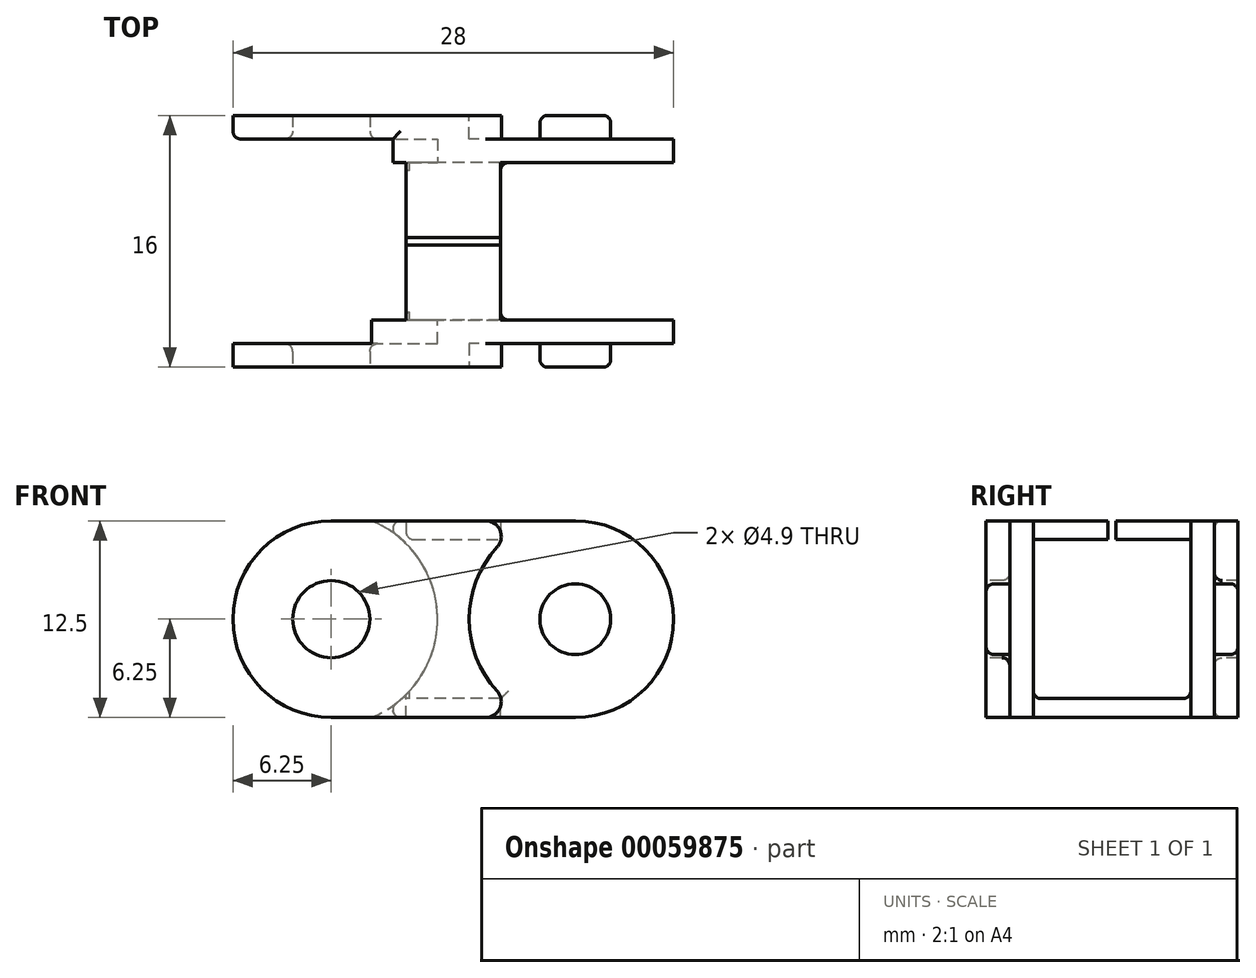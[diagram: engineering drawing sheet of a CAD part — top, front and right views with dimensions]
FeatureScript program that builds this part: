
annotation { "Feature Type Name" : "Feature", "Feature Type Description" : "" }
export const myFeature = defineFeature(function(context is Context, id is Id, definition is map)
    precondition{}
    {
        {
            var Q0;
            Q0=qCreatedBy(makeId("Top.planeOp"),FACE);
            var sketch = newSketch(context, id + "F0", { "sketchPlane" : qUnion([Q0])});
            skLineSegment(sketch, "E0.rect.bottom", {"start": v(14, -8) * mm, "end": v(-14, -8) * mm});
            skLineSegment(sketch, "E0.rect.top", {"start": v(14, 8) * mm, "end": v(-14, 8) * mm});
            skLineSegment(sketch, "E0.rect.left", {"start": v(14, -8) * mm, "end": v(14, 8) * mm});
            skLineSegment(sketch, "E0.rect.right", {"start": v(-14, -8) * mm, "end": v(-14, 8) * mm});
            skPoint(sketch, "E0.rect.middle", {"position": v(0, 0) * mm});
            skSolve(sketch);
        }
        {
            var Q0;
            Q0=qSketchRegion(id+"F0",true);
            extrude(context, id + "F1", {"entities" : qUnion([Q0]), "endBound" : BoundingType.SYMMETRIC, "depth" : 12.5 * mm});
        }
        {
            var Q0;
            Q0=makeQuery(id+"F1.opExtrude","CAP_EDGE",EDGE,{"disambiguationData":[OSD([sQuery(id+"F0.wireOp",EDGE,"E0.rect.right")])],"isStart":false});
            var Q1;
            Q1=makeQuery(id+"F1.opExtrude","CAP_EDGE",EDGE,{"disambiguationData":[OSD([sQuery(id+"F0.wireOp",EDGE,"E0.rect.right")])],"isStart":true});
            var Q2;
            Q2=makeQuery(id+"F1.opExtrude","CAP_EDGE",EDGE,{"disambiguationData":[OSD([sQuery(id+"F0.wireOp",EDGE,"E0.rect.left")])],"isStart":false});
            var Q3;
            Q3=makeQuery(id+"F1.opExtrude","CAP_EDGE",EDGE,{"disambiguationData":[OSD([sQuery(id+"F0.wireOp",EDGE,"E0.rect.left")])],"isStart":true});
            fillet(context, id + "F2", {"entities" : qUnion([Q0, Q1, Q2, Q3]), "radius" : 6.25 * mm, "tangentPropagation" : true, "allowEdgeOverflow" : false});
        }
        {
            var Q0;
            Q0=makeQuery(id+"F1.opExtrude","CAP_FACE",FACE,{"disambiguationData":[OSD([sQuery(id+"F0.wireOp",EDGE,"E0.rect.bottom"),sQuery(id+"F0.wireOp",EDGE,"E0.rect.top"),sQuery(id+"F0.wireOp",EDGE,"E0.rect.left"),sQuery(id+"F0.wireOp",EDGE,"E0.rect.right")])],"isStart":false});
            var Q1;
            {var subQ0=sQuery(id+"F0.wireOp",EDGE,"E0.rect.right");Q1=makeQuery(id+"F2.opFillet","BLEND_FACE",FACE,{"disambiguationData":[OSD([subQ0]),TDD([makeQuery(id+"F1.opExtrude","CAP_EDGE",EDGE,{"disambiguationData":[OSD([subQ0])],"isStart":false})])]});}
            var Q2;
            Q2=makeQuery(id+"F1.opExtrude","SWEPT_FACE",FACE,{"disambiguationData":[OSD([sQuery(id+"F0.wireOp",EDGE,"E0.rect.right")])]});
            var Q3;
            {var subQ0=sQuery(id+"F0.wireOp",EDGE,"E0.rect.right");Q3=makeQuery(id+"F2.opFillet","BLEND_FACE",FACE,{"disambiguationData":[OSD([subQ0]),TDD([makeQuery(id+"F1.opExtrude","CAP_EDGE",EDGE,{"disambiguationData":[OSD([subQ0])],"isStart":true})])]});}
            var Q4;
            {var subQ0=sQuery(id+"F0.wireOp",EDGE,"E0.rect.left");Q4=makeQuery(id+"F2.opFillet","BLEND_FACE",FACE,{"disambiguationData":[OSD([subQ0]),TDD([makeQuery(id+"F1.opExtrude","CAP_EDGE",EDGE,{"disambiguationData":[OSD([subQ0])],"isStart":false})])]});}
            var Q5;
            Q5=makeQuery(id+"F1.opExtrude","SWEPT_FACE",FACE,{"disambiguationData":[OSD([sQuery(id+"F0.wireOp",EDGE,"E0.rect.left")])]});
            var Q6;
            {var subQ0=sQuery(id+"F0.wireOp",EDGE,"E0.rect.left");Q6=makeQuery(id+"F2.opFillet","BLEND_FACE",FACE,{"disambiguationData":[OSD([subQ0]),TDD([makeQuery(id+"F1.opExtrude","CAP_EDGE",EDGE,{"disambiguationData":[OSD([subQ0])],"isStart":true})])]});}
            shell(context, id + "F3", {"entities" : qUnion([Q0, Q1, Q2, Q3, Q4, Q5, Q6]), "thickness" : 3 * mm});
        }
        {
            var Q0;
            {var subQ0=sQuery(id+"F0.wireOp",EDGE,"E0.rect.bottom");var subQ1=sQuery(id+"F0.wireOp",EDGE,"E0.rect.top");var subQ2=sQuery(id+"F0.wireOp",EDGE,"E0.rect.left");var subQ3=sQuery(id+"F0.wireOp",EDGE,"E0.rect.right");Q0=makeQuery(id+"F3.opShell","OFFSET_FACE",FACE,{"disambiguationData":[OSD([subQ0,subQ1,subQ2,subQ3]),TDD([makeQuery(id+"F1.opExtrude","CAP_FACE",FACE,{"disambiguationData":[OSD([subQ0,subQ1,subQ2,subQ3])],"isStart":true})])]});}
            var sketch = newSketch(context, id + "F4", { "sketchPlane" : qUnion([Q0])});
            skLineSegment(sketch, "E1.bottom", {"start": v(-7.75, -5) * mm, "end": v(-3, -5) * mm});
            skLineSegment(sketch, "E1.top", {"start": v(-7.75, 5) * mm, "end": v(-3, 5) * mm});
            skLineSegment(sketch, "E1.left", {"start": v(-7.75, -5) * mm, "end": v(-7.75, 5) * mm});
            skLineSegment(sketch, "E1.right", {"start": v(-3, -5) * mm, "end": v(-3, 5) * mm});
            skLineSegment(sketch, "E2.bottom", {"start": v(7.75, -5) * mm, "end": v(3, -5) * mm});
            skLineSegment(sketch, "E2.top", {"start": v(7.75, 5) * mm, "end": v(3, 5) * mm});
            skLineSegment(sketch, "E2.left", {"start": v(7.75, -5) * mm, "end": v(7.75, 5) * mm});
            skLineSegment(sketch, "E2.right", {"start": v(3, -5) * mm, "end": v(3, 5) * mm});
            skSolve(sketch);
        }
        {
            var Q0;
            Q0=qSketchRegion(id+"F4",true);
            extrude(context, id + "F5", {"entities" : qUnion([Q0]), "operationType" : NewBodyOperationType.REMOVE, "oppositeDirection" : true, "depth" : 25 * mm});
        }
        {
            var Q0;
            Q0=makeQuery(id+"F5.boolean.opBoolean","COPY",FACE,{"derivedFrom":makeQuery(id+"F5.opExtrude","SWEPT_FACE",FACE,{"disambiguationData":[OSD([sQuery(id+"F4.wireOp",EDGE,"E1.right")])]})});
            var sketch = newSketch(context, id + "F6", { "sketchPlane" : qUnion([Q0])});
            skLineSegment(sketch, "E3.bottom", {"start": v(-5, -3.25) * mm, "end": v(5, -3.25) * mm});
            skLineSegment(sketch, "E3.top", {"start": v(-5, -5.05) * mm, "end": v(5, -5.05) * mm});
            skLineSegment(sketch, "E3.left", {"start": v(-5, -3.25) * mm, "end": v(-5, -5.05) * mm});
            skLineSegment(sketch, "E3.right", {"start": v(5, -3.25) * mm, "end": v(5, -5.05) * mm});
            skSolve(sketch);
        }
        {
            var Q0;
            Q0=qSketchRegion(id+"F6",true);
            extrude(context, id + "F7", {"entities" : qUnion([Q0]), "operationType" : NewBodyOperationType.REMOVE, "oppositeDirection" : true, "depth" : 25 * mm});
        }
        {
            var Q0;
            Q0=makeQuery(id+"F1.opExtrude","CAP_FACE",FACE,{"disambiguationData":[OSD([sQuery(id+"F0.wireOp",EDGE,"E0.rect.bottom"),sQuery(id+"F0.wireOp",EDGE,"E0.rect.top"),sQuery(id+"F0.wireOp",EDGE,"E0.rect.left"),sQuery(id+"F0.wireOp",EDGE,"E0.rect.right")])],"isStart":false});
            var sketch = newSketch(context, id + "F8", { "sketchPlane" : qUnion([Q0])});
            skLineSegment(sketch, "E4.bottom", {"start": v(-3, 5) * mm, "end": v(3, 5) * mm});
            skLineSegment(sketch, "E4.top", {"start": v(-3, -5) * mm, "end": v(3, -5) * mm});
            skLineSegment(sketch, "E4.left", {"start": v(-3, 5) * mm, "end": v(-3, -5) * mm});
            skLineSegment(sketch, "E4.right", {"start": v(3, 5) * mm, "end": v(3, -5) * mm});
            skSolve(sketch);
        }
        {
            var Q0;
            Q0=qSketchRegion(id+"F8",true);
            extrude(context, id + "F9", {"entities" : qUnion([Q0]), "operationType" : NewBodyOperationType.ADD, "oppositeDirection" : true, "depth" : 1.2 * mm});
        }
        {
            var Q0;
            Q0=makeQuery(id+"F1.opExtrude","SWEPT_FACE",FACE,{"disambiguationData":[OSD([sQuery(id+"F0.wireOp",EDGE,"E0.rect.bottom")])]});
            var sketch = newSketch(context, id + "F10", { "sketchPlane" : qUnion([Q0])});
            skCircle(sketch, "E5", {"center": v(7.75, 0) * mm, "radius": 6.75 * mm});
            skSolve(sketch);
        }
        {
            var Q0;
            Q0=qSketchRegion(id+"F10",true);
            extrude(context, id + "F11", {"entities" : qUnion([Q0]), "operationType" : NewBodyOperationType.REMOVE, "oppositeDirection" : true, "depth" : 1.5 * mm});
        }
        {
            var Q0;
            Q0=makeQuery(id+"F1.opExtrude","SWEPT_FACE",FACE,{"disambiguationData":[OSD([sQuery(id+"F0.wireOp",EDGE,"E0.rect.top")])]});
            var sketch = newSketch(context, id + "F12", { "sketchPlane" : qUnion([Q0])});
            skCircle(sketch, "E6", {"center": v(-7.75, 0) * mm, "radius": 6.75 * mm});
            skSolve(sketch);
        }
        {
            var Q0;
            Q0=qSketchRegion(id+"F12",true);
            extrude(context, id + "F13", {"entities" : qUnion([Q0]), "operationType" : NewBodyOperationType.REMOVE, "oppositeDirection" : true, "depth" : 1.5 * mm});
        }
        {
            var Q0;
            {var subQ0=sQuery(id+"F0.wireOp",EDGE,"E0.rect.bottom");var subQ1=sQuery(id+"F0.wireOp",EDGE,"E0.rect.top");var subQ2=sQuery(id+"F0.wireOp",EDGE,"E0.rect.left");var subQ3=sQuery(id+"F0.wireOp",EDGE,"E0.rect.right");var subQ4=makeQuery(id+"F1.opExtrude","CAP_FACE",FACE,{"disambiguationData":[OSD([subQ0,subQ1,subQ2,subQ3])],"isStart":false});Q0=makeQuery(id+"F11.boolean.opBoolean","INTERSECT",EDGE,{"derivedFrom":[makeQuery(id+"FRDs2wFj56Co6Q4_1.boolean.opBoolean","MERGE",FACE,{"derivedFrom":[makeQuery(id+"F3.opShell","OFFSET_FACE",FACE,{"disambiguationData":[OSD([subQ0,subQ1,subQ2,subQ3]),TDD([subQ4])]}),subQ4,makeQuery(id+"FRDs2wFj56Co6Q4_1.opExtrude","CAP_FACE",FACE,{"disambiguationData":[OSD([sQuery(id+"F8wkNr267Ss34zO_1.wireOp",EDGE,"6609082b-c965-4ff1-a180-b40e3fbcedff.bottom"),sQuery(id+"F8wkNr267Ss34zO_1.wireOp",EDGE,"6609082b-c965-4ff1-a180-b40e3fbcedff.top"),sQuery(id+"F8wkNr267Ss34zO_1.wireOp",EDGE,"6609082b-c965-4ff1-a180-b40e3fbcedff.left"),sQuery(id+"F8wkNr267Ss34zO_1.wireOp",EDGE,"6609082b-c965-4ff1-a180-b40e3fbcedff.right")])],"isStart":true})]}),makeQuery(id+"F11.opExtrude","SWEPT_FACE",FACE,{"disambiguationData":[OSD([sQuery(id+"F10.wireOp",EDGE,"E5")])]})]});}
            var Q1;
            Q1=makeQuery(id+"F11.boolean.opBoolean","INTERSECT",EDGE,{"derivedFrom":[makeQuery(id+"F1.opExtrude","CAP_FACE",FACE,{"disambiguationData":[OSD([sQuery(id+"F0.wireOp",EDGE,"E0.rect.bottom"),sQuery(id+"F0.wireOp",EDGE,"E0.rect.top"),sQuery(id+"F0.wireOp",EDGE,"E0.rect.left"),sQuery(id+"F0.wireOp",EDGE,"E0.rect.right")])],"isStart":true}),makeQuery(id+"F11.opExtrude","SWEPT_FACE",FACE,{"disambiguationData":[OSD([sQuery(id+"F10.wireOp",EDGE,"E5")])]})]});
            var Q2;
            {var subQ0=sQuery(id+"F0.wireOp",EDGE,"E0.rect.bottom");var subQ1=sQuery(id+"F0.wireOp",EDGE,"E0.rect.top");var subQ2=sQuery(id+"F0.wireOp",EDGE,"E0.rect.left");var subQ3=sQuery(id+"F0.wireOp",EDGE,"E0.rect.right");var subQ4=makeQuery(id+"F1.opExtrude","CAP_FACE",FACE,{"disambiguationData":[OSD([subQ0,subQ1,subQ2,subQ3])],"isStart":false});Q2=makeQuery(id+"F13.boolean.opBoolean","INTERSECT",EDGE,{"derivedFrom":[makeQuery(id+"FRDs2wFj56Co6Q4_1.boolean.opBoolean","MERGE",FACE,{"derivedFrom":[makeQuery(id+"F3.opShell","OFFSET_FACE",FACE,{"disambiguationData":[OSD([subQ0,subQ1,subQ2,subQ3]),TDD([subQ4])]}),subQ4,makeQuery(id+"FRDs2wFj56Co6Q4_1.opExtrude","CAP_FACE",FACE,{"disambiguationData":[OSD([sQuery(id+"F8wkNr267Ss34zO_1.wireOp",EDGE,"6609082b-c965-4ff1-a180-b40e3fbcedff.bottom"),sQuery(id+"F8wkNr267Ss34zO_1.wireOp",EDGE,"6609082b-c965-4ff1-a180-b40e3fbcedff.top"),sQuery(id+"F8wkNr267Ss34zO_1.wireOp",EDGE,"6609082b-c965-4ff1-a180-b40e3fbcedff.left"),sQuery(id+"F8wkNr267Ss34zO_1.wireOp",EDGE,"6609082b-c965-4ff1-a180-b40e3fbcedff.right")])],"isStart":true})]}),makeQuery(id+"F13.opExtrude","SWEPT_FACE",FACE,{"disambiguationData":[OSD([sQuery(id+"F12.wireOp",EDGE,"E6")])]})]});}
            var Q3;
            Q3=makeQuery(id+"F13.boolean.opBoolean","INTERSECT",EDGE,{"derivedFrom":[makeQuery(id+"F1.opExtrude","CAP_FACE",FACE,{"disambiguationData":[OSD([sQuery(id+"F0.wireOp",EDGE,"E0.rect.bottom"),sQuery(id+"F0.wireOp",EDGE,"E0.rect.top"),sQuery(id+"F0.wireOp",EDGE,"E0.rect.left"),sQuery(id+"F0.wireOp",EDGE,"E0.rect.right")])],"isStart":true}),makeQuery(id+"F13.opExtrude","SWEPT_FACE",FACE,{"disambiguationData":[OSD([sQuery(id+"F12.wireOp",EDGE,"E6")])]})]});
            var Q4;
            {var subQ0=sQuery(id+"F0.wireOp",EDGE,"E0.rect.left");var subQ1=sQuery(id+"F0.wireOp",EDGE,"E0.rect.bottom");var subQ2=sQuery(id+"F0.wireOp",EDGE,"E0.rect.top");var subQ3=sQuery(id+"F0.wireOp",EDGE,"E0.rect.right");var subQ4=makeQuery(id+"F1.opExtrude","CAP_FACE",FACE,{"disambiguationData":[OSD([subQ1,subQ2,subQ0,subQ3])],"isStart":false});Q4=makeQuery(id+"F11.boolean.opBoolean","SPLIT",EDGE,{"disambiguationData":[TD([makeQuery(id+"F1.opExtrude","SWEPT_FACE",FACE,{"disambiguationData":[OSD([subQ1])]})])],"derivedFrom":makeQuery(id+"F2.opFillet","BLEND_EDGE",EDGE,{"blendedFrom":[makeQuery(id+"F1.opExtrude","CAP_EDGE",EDGE,{"disambiguationData":[OSD([subQ0])],"isStart":false}),subQ4],"blendedInto":[subQ4]})});}
            var Q5;
            {var subQ0=sQuery(id+"F0.wireOp",EDGE,"E0.rect.bottom");var subQ1=sQuery(id+"F0.wireOp",EDGE,"E0.rect.top");var subQ2=sQuery(id+"F0.wireOp",EDGE,"E0.rect.left");var subQ3=sQuery(id+"F0.wireOp",EDGE,"E0.rect.right");var subQ4=makeQuery(id+"F1.opExtrude","CAP_FACE",FACE,{"disambiguationData":[OSD([subQ0,subQ1,subQ2,subQ3])],"isStart":true});Q5=makeQuery(id+"F11.boolean.opBoolean","SPLIT",EDGE,{"disambiguationData":[TD([makeQuery(id+"F1.opExtrude","SWEPT_FACE",FACE,{"disambiguationData":[OSD([subQ0])]})])],"derivedFrom":makeQuery(id+"F3.opShell","OFFSET_EDGE",EDGE,{"disambiguationData":[OSD([subQ0,subQ1,subQ2,subQ3]),TDD([makeQuery(id+"F2.opFillet","BLEND_EDGE",EDGE,{"blendedFrom":[makeQuery(id+"F1.opExtrude","CAP_EDGE",EDGE,{"disambiguationData":[OSD([subQ2])],"isStart":true}),subQ4],"blendedInto":[subQ4]})]),OD(0.0)]})});}
            var Q6;
            {var subQ0=sQuery(id+"F0.wireOp",EDGE,"E0.rect.bottom");var subQ1=sQuery(id+"F0.wireOp",EDGE,"E0.rect.top");var subQ2=sQuery(id+"F0.wireOp",EDGE,"E0.rect.left");var subQ3=sQuery(id+"F0.wireOp",EDGE,"E0.rect.right");var subQ4=makeQuery(id+"F1.opExtrude","CAP_FACE",FACE,{"disambiguationData":[OSD([subQ0,subQ1,subQ2,subQ3])],"isStart":false});Q6=makeQuery(id+"F13.boolean.opBoolean","SPLIT",EDGE,{"disambiguationData":[TD([makeQuery(id+"F1.opExtrude","SWEPT_FACE",FACE,{"disambiguationData":[OSD([subQ1])]})])],"derivedFrom":makeQuery(id+"F3.opShell","OFFSET_EDGE",EDGE,{"disambiguationData":[OSD([subQ0,subQ1,subQ2,subQ3]),TDD([makeQuery(id+"F2.opFillet","BLEND_EDGE",EDGE,{"blendedFrom":[makeQuery(id+"F1.opExtrude","CAP_EDGE",EDGE,{"disambiguationData":[OSD([subQ2])],"isStart":false}),subQ4],"blendedInto":[subQ4]})])]})});}
            var Q7;
            {var subQ0=sQuery(id+"F0.wireOp",EDGE,"E0.rect.left");var subQ1=sQuery(id+"F0.wireOp",EDGE,"E0.rect.top");var subQ2=makeQuery(id+"F1.opExtrude","CAP_FACE",FACE,{"disambiguationData":[OSD([sQuery(id+"F0.wireOp",EDGE,"E0.rect.bottom"),subQ1,subQ0,sQuery(id+"F0.wireOp",EDGE,"E0.rect.right")])],"isStart":true});Q7=makeQuery(id+"F13.boolean.opBoolean","SPLIT",EDGE,{"disambiguationData":[TD([makeQuery(id+"F1.opExtrude","SWEPT_FACE",FACE,{"disambiguationData":[OSD([subQ1])]})])],"derivedFrom":makeQuery(id+"F2.opFillet","BLEND_EDGE",EDGE,{"blendedFrom":[makeQuery(id+"F1.opExtrude","CAP_EDGE",EDGE,{"disambiguationData":[OSD([subQ0])],"isStart":true}),subQ2],"blendedInto":[subQ2]})});}
            fillet(context, id + "F14", {"entities" : qUnion([Q0, Q1, Q2, Q3, Q4, Q5, Q6, Q7]), "radius" : 1 * mm, "tangentPropagation" : true, "allowEdgeOverflow" : false});
        }
        {
            var Q0;
            Q0=makeQuery(id+"F11.boolean.opBoolean","COPY",FACE,{"derivedFrom":makeQuery(id+"F11.opExtrude","CAP_FACE",FACE,{"disambiguationData":[OSD([sQuery(id+"F10.wireOp",EDGE,"E5")])],"isStart":false})});
            var sketch = newSketch(context, id + "F15", { "sketchPlane" : qUnion([Q0])});
            skCircle(sketch, "E7", {"center": v(7.75, 0) * mm, "radius": 2.25 * mm});
            skSolve(sketch);
        }
        {
            var Q0;
            Q0=qSketchRegion(id+"F15",true);
            extrude(context, id + "F16", {"entities" : qUnion([Q0]), "operationType" : NewBodyOperationType.ADD, "depth" : 1.5 * mm});
        }
        {
            var Q0;
            Q0=makeQuery(id+"F13.boolean.opBoolean","COPY",FACE,{"derivedFrom":makeQuery(id+"F13.opExtrude","CAP_FACE",FACE,{"disambiguationData":[OSD([sQuery(id+"F12.wireOp",EDGE,"E6")])],"isStart":false})});
            var sketch = newSketch(context, id + "F17", { "sketchPlane" : qUnion([Q0])});
            skCircle(sketch, "E8", {"center": v(-7.75, 0) * mm, "radius": 2.25 * mm});
            skSolve(sketch);
        }
        {
            var Q0;
            Q0=qSketchRegion(id+"F17",true);
            extrude(context, id + "F18", {"entities" : qUnion([Q0]), "operationType" : NewBodyOperationType.ADD, "depth" : 1.5 * mm});
        }
        {
            var Q0;
            Q0=makeQuery(id+"F1.opExtrude","SWEPT_FACE",FACE,{"disambiguationData":[OSD([sQuery(id+"F0.wireOp",EDGE,"E0.rect.bottom")])]});
            var sketch = newSketch(context, id + "F19", { "sketchPlane" : qUnion([Q0])});
            skCircle(sketch, "E9", {"center": v(-7.75, 0) * mm, "radius": 2.45 * mm});
            skSolve(sketch);
        }
        {
            var Q0;
            Q0=qSketchRegion(id+"F19",true);
            extrude(context, id + "F20", {"entities" : qUnion([Q0]), "operationType" : NewBodyOperationType.REMOVE, "endBound" : BoundingType.THROUGH_ALL, "oppositeDirection" : true, "depth" : 25 * mm});
        }
        {
            var Q0;
            Q0=makeQuery(id+"FHNYXm6BuEGCrrz_1.boolean.opBoolean","MERGE",FACE,{"derivedFrom":[makeQuery(id+"F3.opShell","OFFSET_FACE",FACE,{"disambiguationData":[OSD([sQuery(id+"F0.wireOp",EDGE,"E0.rect.top")])]}),makeQuery(id+"FHNYXm6BuEGCrrz_1.opExtrude","SWEPT_FACE",FACE,{"disambiguationData":[OSD([sQuery(id+"FrscQX9RS2ccQFD_1.wireOp",EDGE,"376541ee-2e4d-4804-9836-3ca692176c24.right")])]})]});
            var sketch = newSketch(context, id + "F21", { "sketchPlane" : qUnion([Q0])});
            skCircle(sketch, "E10", {"center": v(-7.75, 0) * mm, "radius": 6.75 * mm});
            skSolve(sketch);
        }
        {
            var Q0;
            Q0=qSketchRegion(id+"F21",true);
            extrude(context, id + "F22", {"entities" : qUnion([Q0]), "operationType" : NewBodyOperationType.REMOVE, "oppositeDirection" : true, "depth" : 1.5 * mm});
        }
        {
            var Q0;
            Q0=makeQuery(id+"FHNYXm6BuEGCrrz_1.boolean.opBoolean","MERGE",FACE,{"derivedFrom":[makeQuery(id+"F3.opShell","OFFSET_FACE",FACE,{"disambiguationData":[OSD([sQuery(id+"F0.wireOp",EDGE,"E0.rect.bottom")])]}),makeQuery(id+"FHNYXm6BuEGCrrz_1.opExtrude","SWEPT_FACE",FACE,{"disambiguationData":[OSD([sQuery(id+"FrscQX9RS2ccQFD_1.wireOp",EDGE,"376541ee-2e4d-4804-9836-3ca692176c24.left")])]})]});
            var sketch = newSketch(context, id + "F23", { "sketchPlane" : qUnion([Q0])});
            skCircle(sketch, "E11", {"center": v(7.75, 0) * mm, "radius": 6.75 * mm});
            skSolve(sketch);
        }
        {
            var Q0;
            Q0=qSketchRegion(id+"F23",true);
            extrude(context, id + "F24", {"entities" : qUnion([Q0]), "operationType" : NewBodyOperationType.REMOVE, "oppositeDirection" : true, "depth" : 1.5 * mm});
        }
        {
            var Q0;
            {var subQ0=sQuery(id+"F0.wireOp",EDGE,"E0.rect.bottom");var subQ1=sQuery(id+"F0.wireOp",EDGE,"E0.rect.top");var subQ2=sQuery(id+"F0.wireOp",EDGE,"E0.rect.left");var subQ3=sQuery(id+"F0.wireOp",EDGE,"E0.rect.right");var subQ4=makeQuery(id+"F1.opExtrude","CAP_FACE",FACE,{"disambiguationData":[OSD([subQ0,subQ1,subQ2,subQ3])],"isStart":false});Q0=makeQuery(id+"F22.boolean.opBoolean","INTERSECT",EDGE,{"derivedFrom":[makeQuery(id+"FRDs2wFj56Co6Q4_1.boolean.opBoolean","MERGE",FACE,{"derivedFrom":[makeQuery(id+"F3.opShell","OFFSET_FACE",FACE,{"disambiguationData":[OSD([subQ0,subQ1,subQ2,subQ3]),TDD([subQ4])]}),subQ4,makeQuery(id+"FRDs2wFj56Co6Q4_1.opExtrude","CAP_FACE",FACE,{"disambiguationData":[OSD([sQuery(id+"F8wkNr267Ss34zO_1.wireOp",EDGE,"6609082b-c965-4ff1-a180-b40e3fbcedff.bottom"),sQuery(id+"F8wkNr267Ss34zO_1.wireOp",EDGE,"6609082b-c965-4ff1-a180-b40e3fbcedff.top"),sQuery(id+"F8wkNr267Ss34zO_1.wireOp",EDGE,"6609082b-c965-4ff1-a180-b40e3fbcedff.left"),sQuery(id+"F8wkNr267Ss34zO_1.wireOp",EDGE,"6609082b-c965-4ff1-a180-b40e3fbcedff.right")])],"isStart":true})]}),makeQuery(id+"F22.opExtrude","SWEPT_FACE",FACE,{"disambiguationData":[OSD([sQuery(id+"F21.wireOp",EDGE,"E10")])]})]});}
            var Q1;
            Q1=makeQuery(id+"F22.boolean.opBoolean","INTERSECT",EDGE,{"derivedFrom":[makeQuery(id+"F1.opExtrude","CAP_FACE",FACE,{"disambiguationData":[OSD([sQuery(id+"F0.wireOp",EDGE,"E0.rect.bottom"),sQuery(id+"F0.wireOp",EDGE,"E0.rect.top"),sQuery(id+"F0.wireOp",EDGE,"E0.rect.left"),sQuery(id+"F0.wireOp",EDGE,"E0.rect.right")])],"isStart":true}),makeQuery(id+"F22.opExtrude","SWEPT_FACE",FACE,{"disambiguationData":[OSD([sQuery(id+"F21.wireOp",EDGE,"E10")])]})]});
            var Q2;
            {var subQ0=sQuery(id+"F0.wireOp",EDGE,"E0.rect.bottom");var subQ1=sQuery(id+"F0.wireOp",EDGE,"E0.rect.top");var subQ2=sQuery(id+"F0.wireOp",EDGE,"E0.rect.left");var subQ3=sQuery(id+"F0.wireOp",EDGE,"E0.rect.right");var subQ4=makeQuery(id+"F1.opExtrude","CAP_FACE",FACE,{"disambiguationData":[OSD([subQ0,subQ1,subQ2,subQ3])],"isStart":false});Q2=makeQuery(id+"F22.boolean.opBoolean","INTERSECT",EDGE,{"derivedFrom":[makeQuery(id+"FRDs2wFj56Co6Q4_1.boolean.opBoolean","MERGE",FACE,{"derivedFrom":[makeQuery(id+"F3.opShell","OFFSET_FACE",FACE,{"disambiguationData":[OSD([subQ0,subQ1,subQ2,subQ3]),TDD([subQ4])]}),subQ4,makeQuery(id+"FRDs2wFj56Co6Q4_1.opExtrude","CAP_FACE",FACE,{"disambiguationData":[OSD([sQuery(id+"F8wkNr267Ss34zO_1.wireOp",EDGE,"6609082b-c965-4ff1-a180-b40e3fbcedff.bottom"),sQuery(id+"F8wkNr267Ss34zO_1.wireOp",EDGE,"6609082b-c965-4ff1-a180-b40e3fbcedff.top"),sQuery(id+"F8wkNr267Ss34zO_1.wireOp",EDGE,"6609082b-c965-4ff1-a180-b40e3fbcedff.left"),sQuery(id+"F8wkNr267Ss34zO_1.wireOp",EDGE,"6609082b-c965-4ff1-a180-b40e3fbcedff.right")])],"isStart":true})]}),makeQuery(id+"F22.opExtrude","CAP_FACE",FACE,{"disambiguationData":[OSD([sQuery(id+"F21.wireOp",EDGE,"E10")])],"isStart":false})]});}
            var Q3;
            Q3=makeQuery(id+"F22.boolean.opBoolean","INTERSECT",EDGE,{"derivedFrom":[makeQuery(id+"F3.opShell","OFFSET_FACE",FACE,{"disambiguationData":[OSD([sQuery(id+"F0.wireOp",EDGE,"E0.rect.right")])]}),makeQuery(id+"F22.opExtrude","CAP_FACE",FACE,{"disambiguationData":[OSD([sQuery(id+"F21.wireOp",EDGE,"E10")])],"isStart":false})]});
            fillet(context, id + "F25", {"entities" : qUnion([Q0, Q1, Q2, Q3]), "radius" : 0.5 * mm, "tangentPropagation" : true, "allowEdgeOverflow" : false});
        }
        {
            var Q0;
            Q0=makeQuery(id+"F7.boolean.opBoolean","COPY",EDGE,{"derivedFrom":makeQuery(id+"F7.opExtrude","CAP_EDGE",EDGE,{"disambiguationData":[OSD([sQuery(id+"F6.wireOp",EDGE,"E3.top")])],"isStart":true})});
            var Q1;
            Q1=makeQuery(id+"F9.opExtrude","CAP_EDGE",EDGE,{"disambiguationData":[OSD([sQuery(id+"F8.wireOp",EDGE,"E4.left")])],"isStart":false});
            fillet(context, id + "F26", {"entities" : qUnion([Q0, Q1]), "radius" : 0.5 * mm, "allowEdgeOverflow" : false});
        }
        {
            var Q0;
            {var subQ0=sQuery(id+"F0.wireOp",EDGE,"E0.rect.bottom");var subQ1=sQuery(id+"F4.wireOp",EDGE,"E1.bottom");var subQ2=sQuery(id+"F6.wireOp",EDGE,"E3.top");var subQ3=sQuery(id+"F6.wireOp",EDGE,"E3.right");Q0=makeQuery(id+"F24.boolean.opBoolean","SPLIT",EDGE,{"disambiguationData":[TD([makeQuery(id+"F5.boolean.opBoolean","COPY",FACE,{"derivedFrom":makeQuery(id+"F5.opExtrude","SWEPT_FACE",FACE,{"disambiguationData":[OSD([sQuery(id+"F4.wireOp",EDGE,"E2.right")])]})})])],"derivedFrom":makeQuery(id+"F7.boolean.opBoolean","COPY",EDGE,{"derivedFrom":makeQuery(id+"F7.opExtrude","SWEPT_EDGE",EDGE,{"disambiguationData":[OSD([subQ0,subQ1,sQuery(id+"F4.wireOp",EDGE,"E1.right"),subQ2,subQ3])]})})});}
            var Q1;
            {var subQ0=sQuery(id+"F8.wireOp",EDGE,"E4.top");var subQ2=sQuery(id+"F8.wireOp",EDGE,"E4.right");Q1=makeQuery(id+"F24.boolean.opBoolean","SPLIT",EDGE,{"disambiguationData":[TD([makeQuery(id+"F9.opExtrude","SWEPT_FACE",FACE,{"disambiguationData":[OSD([subQ2])]})])],"derivedFrom":makeQuery(id+"F9.opExtrude","CAP_EDGE",EDGE,{"disambiguationData":[OSD([subQ0])],"isStart":false})});}
            var Q2;
            {var subQ0=sQuery(id+"F0.wireOp",EDGE,"E0.rect.top");var subQ1=sQuery(id+"F4.wireOp",EDGE,"E1.top");var subQ2=sQuery(id+"F6.wireOp",EDGE,"E3.top");var subQ3=sQuery(id+"F6.wireOp",EDGE,"E3.left");Q2=makeQuery(id+"F22.boolean.opBoolean","SPLIT",EDGE,{"disambiguationData":[TD([makeQuery(id+"F5.boolean.opBoolean","COPY",FACE,{"derivedFrom":makeQuery(id+"F5.opExtrude","SWEPT_FACE",FACE,{"disambiguationData":[OSD([sQuery(id+"F4.wireOp",EDGE,"E2.right")])]})})])],"derivedFrom":makeQuery(id+"F7.boolean.opBoolean","COPY",EDGE,{"derivedFrom":makeQuery(id+"F7.opExtrude","SWEPT_EDGE",EDGE,{"disambiguationData":[OSD([subQ0,subQ1,sQuery(id+"F4.wireOp",EDGE,"E1.right"),subQ2,subQ3])]})})});}
            var Q3;
            {var subQ0=sQuery(id+"F8.wireOp",EDGE,"E4.bottom");var subQ2=sQuery(id+"F8.wireOp",EDGE,"E4.right");Q3=makeQuery(id+"F22.boolean.opBoolean","SPLIT",EDGE,{"disambiguationData":[TD([makeQuery(id+"F9.opExtrude","SWEPT_FACE",FACE,{"disambiguationData":[OSD([subQ2])]})])],"derivedFrom":makeQuery(id+"F9.opExtrude","CAP_EDGE",EDGE,{"disambiguationData":[OSD([subQ0])],"isStart":false})});}
            var Q4;
            Q4=makeQuery(id+"F9.opExtrude","SWEPT_EDGE",EDGE,{"disambiguationData":[OSD([sQuery(id+"F0.wireOp",EDGE,"E0.rect.top"),sQuery(id+"F8.wireOp",EDGE,"E4.bottom"),sQuery(id+"F8.wireOp",EDGE,"E4.right")])]});
            var Q5;
            Q5=makeQuery(id+"F9.opExtrude","SWEPT_EDGE",EDGE,{"disambiguationData":[OSD([sQuery(id+"F8.wireOp",EDGE,"E4.top"),sQuery(id+"F8.wireOp",EDGE,"E4.right")])]});
            var Q6;
            Q6=makeQuery(id+"F5.boolean.opBoolean","COPY",EDGE,{"derivedFrom":makeQuery(id+"F5.opExtrude","SWEPT_EDGE",EDGE,{"disambiguationData":[OSD([sQuery(id+"F0.wireOp",EDGE,"E0.rect.bottom"),sQuery(id+"F4.wireOp",EDGE,"E2.bottom"),sQuery(id+"F4.wireOp",EDGE,"E2.right")])]})});
            var Q7;
            Q7=makeQuery(id+"F5.boolean.opBoolean","COPY",EDGE,{"derivedFrom":makeQuery(id+"F5.opExtrude","SWEPT_EDGE",EDGE,{"disambiguationData":[OSD([sQuery(id+"F0.wireOp",EDGE,"E0.rect.top"),sQuery(id+"F4.wireOp",EDGE,"E2.top"),sQuery(id+"F4.wireOp",EDGE,"E2.right")])]})});
            fillet(context, id + "F27", {"entities" : qUnion([Q0, Q1, Q2, Q3, Q4, Q5, Q6, Q7]), "radius" : 0.5 * mm, "tangentPropagation" : true, "allowEdgeOverflow" : false});
        }
        {
            var Q0;
            Q0=makeQuery(id+"F16.opExtrude","CAP_EDGE",EDGE,{"disambiguationData":[OSD([sQuery(id+"F15.wireOp",EDGE,"E7")])],"isStart":false});
            var Q1;
            Q1=makeQuery(id+"F18.opExtrude","CAP_EDGE",EDGE,{"disambiguationData":[OSD([sQuery(id+"F17.wireOp",EDGE,"E8")])],"isStart":false});
            var Q2;
            Q2=makeQuery(id+"F22.boolean.opBoolean","INTERSECT",EDGE,{"derivedFrom":[makeQuery(id+"F20.boolean.opBoolean","COPY",FACE,{"disambiguationData":[OD(1.0)],"derivedFrom":makeQuery(id+"F20.opExtrude","SWEPT_FACE",FACE,{"disambiguationData":[OSD([sQuery(id+"F19.wireOp",EDGE,"E9")])]})}),makeQuery(id+"F22.opExtrude","CAP_FACE",FACE,{"disambiguationData":[OSD([sQuery(id+"F21.wireOp",EDGE,"E10")])],"isStart":false})]});
            var Q3;
            Q3=makeQuery(id+"F24.boolean.opBoolean","INTERSECT",EDGE,{"derivedFrom":[makeQuery(id+"F20.boolean.opBoolean","COPY",FACE,{"disambiguationData":[OD(0.0)],"derivedFrom":makeQuery(id+"F20.opExtrude","SWEPT_FACE",FACE,{"disambiguationData":[OSD([sQuery(id+"F19.wireOp",EDGE,"E9")])]})}),makeQuery(id+"F24.opExtrude","CAP_FACE",FACE,{"disambiguationData":[OSD([sQuery(id+"F23.wireOp",EDGE,"E11")])],"isStart":false})]});
            fillet(context, id + "F28", {"entities" : qUnion([Q0, Q1, Q2, Q3]), "radius" : 0.5 * mm, "tangentPropagation" : true, "allowEdgeOverflow" : false});
        }
        {
            var Q0;
            {var subQ0=sQuery(id+"F0.wireOp",EDGE,"E0.rect.bottom");var subQ1=sQuery(id+"F0.wireOp",EDGE,"E0.rect.top");var subQ2=sQuery(id+"F0.wireOp",EDGE,"E0.rect.left");var subQ3=sQuery(id+"F0.wireOp",EDGE,"E0.rect.right");var subQ4=makeQuery(id+"F1.opExtrude","CAP_FACE",FACE,{"disambiguationData":[OSD([subQ0,subQ1,subQ2,subQ3])],"isStart":false});Q0=makeQuery(id+"F9.boolean.opBoolean","MERGE",FACE,{"derivedFrom":[makeQuery(id+"F3.opShell","OFFSET_FACE",FACE,{"disambiguationData":[OSD([subQ0,subQ1,subQ2,subQ3]),TDD([subQ4])]}),subQ4,makeQuery(id+"F9.opExtrude","CAP_FACE",FACE,{"disambiguationData":[OSD([sQuery(id+"F8.wireOp",EDGE,"E4.bottom"),sQuery(id+"F8.wireOp",EDGE,"E4.top"),sQuery(id+"F8.wireOp",EDGE,"E4.left"),sQuery(id+"F8.wireOp",EDGE,"E4.right")])],"isStart":true})]});}
            var sketch = newSketch(context, id + "F29", { "sketchPlane" : qUnion([Q0])});
            skLineSegment(sketch, "E12.rect.bottom", {"start": v(5, -0.25) * mm, "end": v(-5, -0.25) * mm});
            skLineSegment(sketch, "E12.rect.top", {"start": v(5, 0.25) * mm, "end": v(-5, 0.25) * mm});
            skLineSegment(sketch, "E12.rect.left", {"start": v(5, -0.25) * mm, "end": v(5, 0.25) * mm});
            skLineSegment(sketch, "E12.rect.right", {"start": v(-5, -0.25) * mm, "end": v(-5, 0.25) * mm});
            skPoint(sketch, "E12.rect.middle", {"position": v(0, 0) * mm});
            skSolve(sketch);
        }
        {
            var Q0;
            Q0=qSketchRegion(id+"F29",true);
            var Q1;
            Q1=makeQuery(id+"F9.opExtrude","CAP_FACE",FACE,{"disambiguationData":[OSD([sQuery(id+"F8.wireOp",EDGE,"E4.bottom"),sQuery(id+"F8.wireOp",EDGE,"E4.top"),sQuery(id+"F8.wireOp",EDGE,"E4.left"),sQuery(id+"F8.wireOp",EDGE,"E4.right")])],"isStart":false});
            extrude(context, id + "F30", {"entities" : qUnion([Q0]), "operationType" : NewBodyOperationType.REMOVE, "endBound" : BoundingType.UP_TO_SURFACE, "oppositeDirection" : true, "endBoundEntityFace" : qUnion([Q1]), "depth" : 25 * mm});
        }
    });
